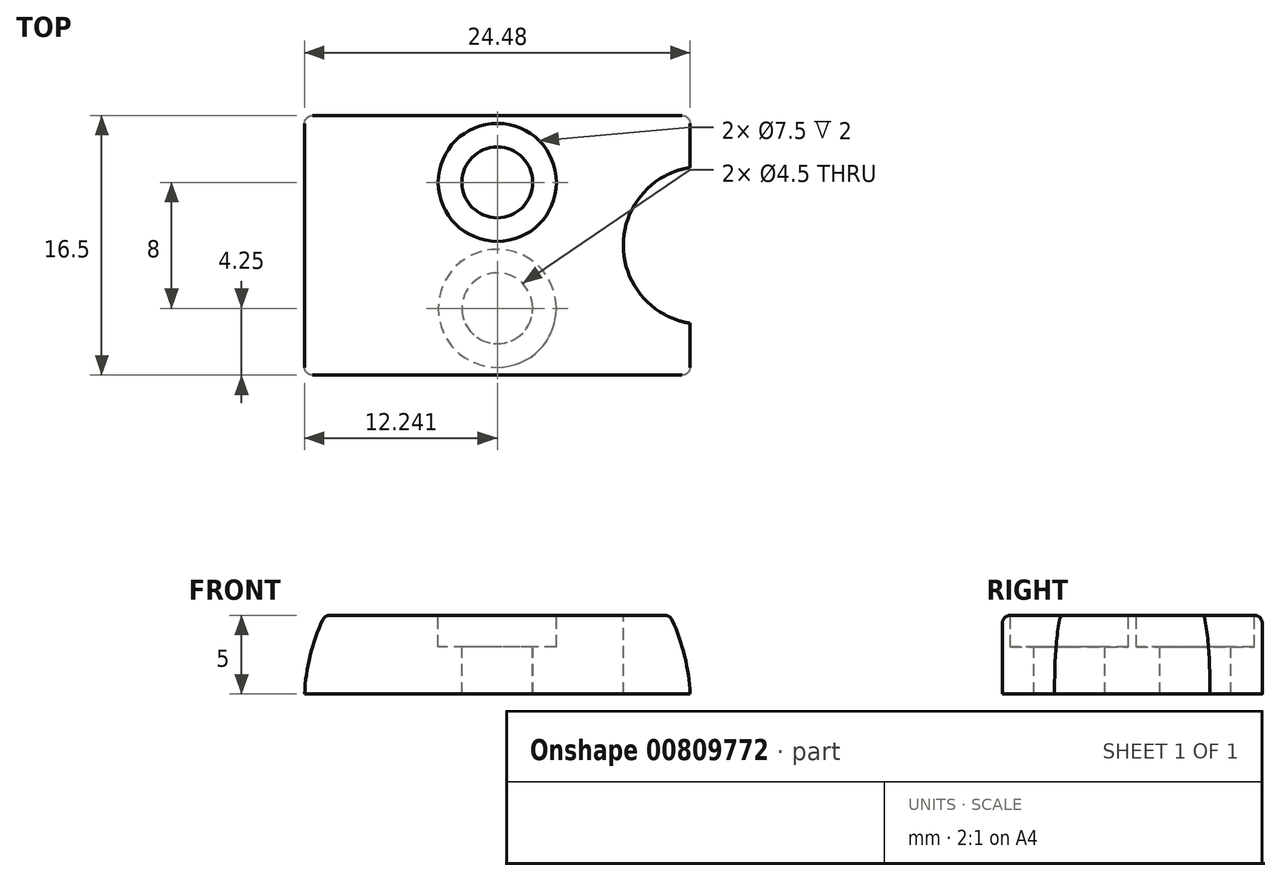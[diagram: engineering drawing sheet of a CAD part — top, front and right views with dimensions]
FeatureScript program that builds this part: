
annotation { "Feature Type Name" : "Feature", "Feature Type Description" : "" }
export const myFeature = defineFeature(function(context is Context, id is Id, definition is map)
    precondition{}
    {
        {
            var Q0;
            Q0=qCreatedBy(makeId("Front.planeOp"),FACE);
            var sketch = newSketch(context, id + "F0", { "sketchPlane" : qUnion([Q0])});
            skLineSegment(sketch, "E0", {"start": v(-15.84, -129.19) * mm, "end": v(0.66, -129.19) * mm});
            skLineSegment(sketch, "E1", {"start": v(0.66, -124.69) * mm, "end": v(0.66, -129.19) * mm});
            skLineSegment(sketch, "E2", {"start": v(-15.34, -124.19) * mm, "end": v(-2.34, -124.19) * mm});
            skArc(sketch, "E3", {"start": v(-15.34, -124.19) * mm, "mid": v(-15.7, -124.34) * mm, "end": v(-15.84, -124.69) * mm});
            skLineSegment(sketch, "E4", {"start": v(-2.34, -124.19) * mm, "end": v(0.16, -124.19) * mm});
            skArc(sketch, "E5", {"start": v(0.66, -124.69) * mm, "mid": v(0.5, -124.34) * mm, "end": v(0.16, -124.19) * mm});
            skLineSegment(sketch, "E6", {"start": v(-5.84, -126.19) * mm, "end": v(-5.84, -129.19) * mm});
            skLineSegment(sketch, "E7", {"start": v(-7.34, -126.19) * mm, "end": v(-7.34, -124.19) * mm});
            skLineSegment(sketch, "E8", {"start": v(-1.34, -126.19) * mm, "end": v(-1.34, -129.19) * mm});
            skLineSegment(sketch, "E9", {"start": v(0.16, -126.19) * mm, "end": v(0.16, -124.19) * mm});
            skLineSegment(sketch, "E10", {"start": v(0.16, -126.19) * mm, "end": v(-7.34, -126.19) * mm});
            skLineSegment(sketch, "E11", {"start": v(-13.84, -126.19) * mm, "end": v(-13.84, -129.19) * mm});
            skLineSegment(sketch, "E12", {"start": v(-15.34, -126.19) * mm, "end": v(-15.34, -124.19) * mm});
            skLineSegment(sketch, "E13", {"start": v(-9.34, -126.19) * mm, "end": v(-9.34, -129.19) * mm});
            skLineSegment(sketch, "E14", {"start": v(-7.84, -126.19) * mm, "end": v(-7.84, -124.19) * mm});
            skLineSegment(sketch, "E15", {"start": v(-15.84, -124.69) * mm, "end": v(-15.84, -129.19) * mm});
            skCircle(sketch, "E16", {"center": v(-77.84, -71.18) * mm, "radius": 3.75 * mm});
            skCircle(sketch, "E17", {"center": v(-77.84, -79.18) * mm, "radius": 3.75 * mm});
            skLineSegment(sketch, "E18", {"start": v(-65.6, -66.93) * mm, "end": v(-65.6, -70.24) * mm});
            skLineSegment(sketch, "E19", {"start": v(-65.6, -80.12) * mm, "end": v(-65.6, -83.43) * mm});
            skLineSegment(sketch, "E20", {"start": v(-90.08, -66.93) * mm, "end": v(-90.08, -83.43) * mm});
            skLineSegment(sketch, "E21", {"start": v(-65.6, -83.43) * mm, "end": v(-90.08, -83.43) * mm});
            skLineSegment(sketch, "E22", {"start": v(-65.6, -66.93) * mm, "end": v(-90.08, -66.93) * mm});
            skLineSegment(sketch, "E23", {"start": v(-66.9, -66.93) * mm, "end": v(-66.9, -70.62) * mm});
            skLineSegment(sketch, "E24", {"start": v(-66.9, -79.74) * mm, "end": v(-66.9, -83.43) * mm});
            skLineSegment(sketch, "E25", {"start": v(-88.78, -66.93) * mm, "end": v(-88.78, -83.43) * mm});
            skCircle(sketch, "E26", {"center": v(-77.84, -71.18) * mm, "radius": 2.25 * mm});
            skCircle(sketch, "E27", {"center": v(-77.84, -79.18) * mm, "radius": 2.25 * mm});
            skArc(sketch, "E28", {"start": v(-65.6, -70.24) * mm, "mid": v(-69.84, -75.18) * mm, "end": v(-65.6, -80.12) * mm});
            skLineSegment(sketch, "E29", {"start": v(-73.09, -129.19) * mm, "end": v(-82.59, -129.19) * mm});
            skLineSegment(sketch, "E30", {"start": v(-88.78, -124.19) * mm, "end": v(-66.9, -124.19) * mm});
            skArc(sketch, "E31", {"start": v(-88.78, -124.19) * mm, "mid": v(-89.7, -126.62) * mm, "end": v(-90.08, -129.19) * mm});
            skArc(sketch, "E32", {"start": v(-65.6, -129.19) * mm, "mid": v(-65.98, -126.62) * mm, "end": v(-66.9, -124.19) * mm});
            skLineSegment(sketch, "E33", {"start": v(-80.09, -126.19) * mm, "end": v(-80.09, -129.19) * mm});
            skLineSegment(sketch, "E34", {"start": v(-75.59, -126.19) * mm, "end": v(-75.59, -129.19) * mm});
            skLineSegment(sketch, "E35", {"start": v(-77.84, -122.19) * mm, "end": v(-77.84, -132.44) * mm});
            skLineSegment(sketch, "E36", {"start": v(-69.84, -124.19) * mm, "end": v(-69.84, -129.19) * mm});
            skLineSegment(sketch, "E37", {"start": v(-81.59, -126.19) * mm, "end": v(-81.59, -124.19) * mm});
            skLineSegment(sketch, "E38", {"start": v(-74.09, -126.19) * mm, "end": v(-74.09, -124.19) * mm});
            skLineSegment(sketch, "E39", {"start": v(-74.09, -126.19) * mm, "end": v(-81.59, -126.19) * mm});
            skLineSegment(sketch, "E40", {"start": v(-12.54, -129.19) * mm, "end": v(-12.54, -124.19) * mm});
            skLineSegment(sketch, "E41", {"start": v(-65.6, -129.19) * mm, "end": v(-90.08, -129.19) * mm});
            skLineSegment(sketch, "E42", {"start": v(-3.6, -122.19) * mm, "end": v(-3.6, -131.02) * mm});
            skLineSegment(sketch, "E43", {"start": v(-2.65, -129.19) * mm, "end": v(-2.65, -124.19) * mm});
            skLineSegment(sketch, "E44", {"start": v(-11.6, -122.19) * mm, "end": v(-11.6, -131.02) * mm});
            skLineSegment(sketch, "E45", {"start": v(-7.84, -126.19) * mm, "end": v(-15.34, -126.19) * mm});
            skLineSegment(sketch, "E46", {"start": v(-77.84, -113.76) * mm, "end": v(-77.84, -145.61) * mm});
            skLineSegment(sketch, "E47", {"start": v(-93.76, -129.69) * mm, "end": v(-61.91, -129.69) * mm});
            skArc(sketch, "E48", {"start": v(-63.6, -129.1) * mm, "mid": v(-64.04, -126.12) * mm, "end": v(-65.1, -123.3) * mm});
            skArc(sketch, "E49", {"start": v(-90.57, -123.3) * mm, "mid": v(-91.63, -126.12) * mm, "end": v(-92.08, -129.1) * mm});
            skArc(sketch, "E50", {"start": v(-63.4, -129.1) * mm, "mid": v(-63.85, -126.07) * mm, "end": v(-64.93, -123.2) * mm});
            skArc(sketch, "E51", {"start": v(-90.75, -123.2) * mm, "mid": v(-91.83, -126.07) * mm, "end": v(-92.28, -129.1) * mm});
            skSolve(sketch);
        }
        {
            var Q0;
            {var subQ0=sQuery(id+"F0.wireOp",EDGE,"E32");Q0=makeQuery(id+"F0.imprint","IMPRINT",FACE,{"disambiguationData":[TD([[makeQuery(id+"F0.imprint","IMPRINT",EDGE,{"derivedFrom":subQ0}),1.0]])]});}
            var Q1;
            {var subQ3=sQuery(id+"F0.wireOp",EDGE,"E34");Q1=makeQuery(id+"F0.imprint","IMPRINT",FACE,{"disambiguationData":[TD([[makeQuery(id+"F0.imprint","IMPRINT",EDGE,{"derivedFrom":subQ3}),1.0]])]});}
            var Q2;
            {var subQ4=sQuery(id+"F0.wireOp",EDGE,"E38");Q2=makeQuery(id+"F0.imprint","IMPRINT",FACE,{"disambiguationData":[TD([[makeQuery(id+"F0.imprint","IMPRINT",EDGE,{"derivedFrom":subQ4}),1.0]])]});}
            var Q3;
            {var subQ0=sQuery(id+"F0.wireOp",EDGE,"E34");Q3=makeQuery(id+"F0.imprint","IMPRINT",FACE,{"disambiguationData":[TD([[makeQuery(id+"F0.imprint","IMPRINT",EDGE,{"derivedFrom":subQ0}),-1.0]])]});}
            var Q4;
            {var subQ0=sQuery(id+"F0.wireOp",EDGE,"E33");Q4=makeQuery(id+"F0.imprint","IMPRINT",FACE,{"disambiguationData":[TD([[makeQuery(id+"F0.imprint","IMPRINT",EDGE,{"derivedFrom":subQ0}),1.0]])]});}
            var Q5;
            {var subQ4=sQuery(id+"F0.wireOp",EDGE,"E37");Q5=makeQuery(id+"F0.imprint","IMPRINT",FACE,{"disambiguationData":[TD([[makeQuery(id+"F0.imprint","IMPRINT",EDGE,{"derivedFrom":subQ4}),-1.0]])]});}
            var Q6;
            {var subQ2=sQuery(id+"F0.wireOp",EDGE,"E31");Q6=makeQuery(id+"F0.imprint","IMPRINT",FACE,{"disambiguationData":[TD([[makeQuery(id+"F0.imprint","IMPRINT",EDGE,{"derivedFrom":subQ2}),1.0]])]});}
            extrude(context, id + "F1", {"entities" : qUnion([Q0, Q1, Q2, Q3, Q4, Q5, Q6]), "depth" : 16.5 * mm, "offsetDistance" : 25 * mm});
        }
        {
            var Q0;
            Q0=makeQuery(id+"F1.opExtrude","SWEPT_FACE",FACE,{"disambiguationData":[OSD([sQuery(id+"F0.wireOp",EDGE,"E30")])]});
            var sketch = newSketch(context, id + "F2", { "sketchPlane" : qUnion([Q0])});
            skCircle(sketch, "E52", {"center": v(-77.84, -4.25) * mm, "radius": 3.75 * mm});
            skCircle(sketch, "E53", {"center": v(-77.84, -12.25) * mm, "radius": 3.75 * mm});
            skLineSegment(sketch, "E54", {"start": v(-65.6, 0) * mm, "end": v(-65.6, -3.3) * mm});
            skLineSegment(sketch, "E55", {"start": v(-65.6, -13.2) * mm, "end": v(-65.6, -16.5) * mm});
            skLineSegment(sketch, "E56", {"start": v(-90.08, 0) * mm, "end": v(-90.08, -16.5) * mm});
            skLineSegment(sketch, "E57", {"start": v(-65.6, -16.5) * mm, "end": v(-90.08, -16.5) * mm});
            skLineSegment(sketch, "E58", {"start": v(-65.6, 0) * mm, "end": v(-90.08, 0) * mm});
            skLineSegment(sketch, "E59", {"start": v(-66.9, 0) * mm, "end": v(-66.9, -3.7) * mm});
            skLineSegment(sketch, "E60", {"start": v(-66.9, -12.8) * mm, "end": v(-66.9, -16.5) * mm});
            skLineSegment(sketch, "E61", {"start": v(-88.78, 0) * mm, "end": v(-88.78, -16.5) * mm});
            skCircle(sketch, "E62", {"center": v(-77.84, -4.25) * mm, "radius": 2.25 * mm});
            skCircle(sketch, "E63", {"center": v(-77.84, -12.25) * mm, "radius": 2.25 * mm});
            skArc(sketch, "E64", {"start": v(-65.6, -3.3) * mm, "mid": v(-69.84, -8.25) * mm, "end": v(-65.6, -13.2) * mm});
            skSolve(sketch);
        }
        {
            var Q0;
            Q0=sQuery(id+"F2.wireOp",VERTEX,"E64.center");
            var Q1;
            Q1=makeQuery(id+"F1.opExtrude","SWEPT_BODY",BODY,{"disambiguationData":[OSD([sQuery(id+"F0.wireOp",EDGE,"E30"),sQuery(id+"F0.wireOp",EDGE,"E31"),sQuery(id+"F0.wireOp",EDGE,"E32"),sQuery(id+"F0.wireOp",EDGE,"E41")])]});
            hole(context, id + "F3", {"style" : HoleStyle.C_BORE, "endStyle" : HoleEndStyle.THROUGH, "holeDiameter" : 5 * mm, "cBoreDiameter" : 10 * mm, "cBoreDepth" : 5 * mm, "majorDiameter" : 5 * mm, "isTappedThrough" : true, "tappedDepth" : 12 * mm, "tapClearance" : 3, "locations" : qUnion([Q0]), "scope" : qUnion([Q1])});
        }
        {
            var Q0;
            Q0=sQuery(id+"F2.wireOp",VERTEX,"E52.center");
            var Q1;
            Q1=sQuery(id+"F2.wireOp",VERTEX,"E53.center");
            var Q2;
            Q2=makeQuery(id+"F1.opExtrude","SWEPT_BODY",BODY,{"disambiguationData":[OSD([sQuery(id+"F0.wireOp",EDGE,"E30"),sQuery(id+"F0.wireOp",EDGE,"E31"),sQuery(id+"F0.wireOp",EDGE,"E32"),sQuery(id+"F0.wireOp",EDGE,"E41")])]});
            hole(context, id + "F4", {"style" : HoleStyle.C_BORE, "endStyle" : HoleEndStyle.THROUGH, "holeDiameter" : 4.5 * mm, "cBoreDiameter" : 7.5 * mm, "cBoreDepth" : 2 * mm, "majorDiameter" : 5 * mm, "isTappedThrough" : true, "tappedDepth" : 12 * mm, "tapClearance" : 3, "locations" : qUnion([Q0, Q1]), "scope" : qUnion([Q2])});
        }
        {
            var Q0;
            Q0=makeQuery(id+"F1.opExtrude","CAP_EDGE",EDGE,{"disambiguationData":[OSD([sQuery(id+"F0.wireOp",EDGE,"E30")])],"isStart":false});
            var Q1;
            Q1=makeQuery(id+"F1.opExtrude","CAP_EDGE",EDGE,{"disambiguationData":[OSD([sQuery(id+"F0.wireOp",EDGE,"E31")])],"isStart":false});
            var Q2;
            Q2=makeQuery(id+"F1.opExtrude","CAP_EDGE",EDGE,{"disambiguationData":[OSD([sQuery(id+"F0.wireOp",EDGE,"E32")])],"isStart":false});
            var Q3;
            {var subQ0=sQuery(id+"F0.wireOp",EDGE,"E30");var subQ1=sQuery(id+"F0.wireOp",EDGE,"E32");Q3=makeQuery(id+"F3.hole-0.boolean.opBoolean","SPLIT",EDGE,{"disambiguationData":[TD([makeQuery(id+"F1.opExtrude","CAP_FACE",FACE,{"disambiguationData":[OSD([subQ0,sQuery(id+"F0.wireOp",EDGE,"E31"),subQ1,sQuery(id+"F0.wireOp",EDGE,"E41")])],"isStart":false})])],"derivedFrom":makeQuery(id+"F1.opExtrude","SWEPT_EDGE",EDGE,{"disambiguationData":[OSD([subQ0,subQ1])]})});}
            var Q4;
            {var subQ0=sQuery(id+"F0.wireOp",EDGE,"E30");var subQ1=sQuery(id+"F0.wireOp",EDGE,"E32");Q4=makeQuery(id+"F3.hole-0.boolean.opBoolean","SPLIT",EDGE,{"disambiguationData":[TD([makeQuery(id+"F1.opExtrude","CAP_FACE",FACE,{"disambiguationData":[OSD([subQ0,sQuery(id+"F0.wireOp",EDGE,"E31"),subQ1,sQuery(id+"F0.wireOp",EDGE,"E41")])],"isStart":true})])],"derivedFrom":makeQuery(id+"F1.opExtrude","SWEPT_EDGE",EDGE,{"disambiguationData":[OSD([subQ0,subQ1])]})});}
            var Q5;
            Q5=makeQuery(id+"F1.opExtrude","CAP_EDGE",EDGE,{"disambiguationData":[OSD([sQuery(id+"F0.wireOp",EDGE,"E32")])],"isStart":true});
            var Q6;
            Q6=makeQuery(id+"F1.opExtrude","CAP_EDGE",EDGE,{"disambiguationData":[OSD([sQuery(id+"F0.wireOp",EDGE,"E30")])],"isStart":true});
            var Q7;
            Q7=makeQuery(id+"F1.opExtrude","CAP_EDGE",EDGE,{"disambiguationData":[OSD([sQuery(id+"F0.wireOp",EDGE,"E31")])],"isStart":true});
            var Q8;
            Q8=makeQuery(id+"F1.opExtrude","SWEPT_EDGE",EDGE,{"disambiguationData":[OSD([sQuery(id+"F0.wireOp",EDGE,"E30"),sQuery(id+"F0.wireOp",EDGE,"E31")])]});
            fillet(context, id + "F5", {"entities" : qUnion([Q0, Q1, Q2, Q3, Q4, Q5, Q6, Q7, Q8]), "radius" : 0.5 * mm, "tangentPropagation" : true, "allowEdgeOverflow" : false});
        }
    });
